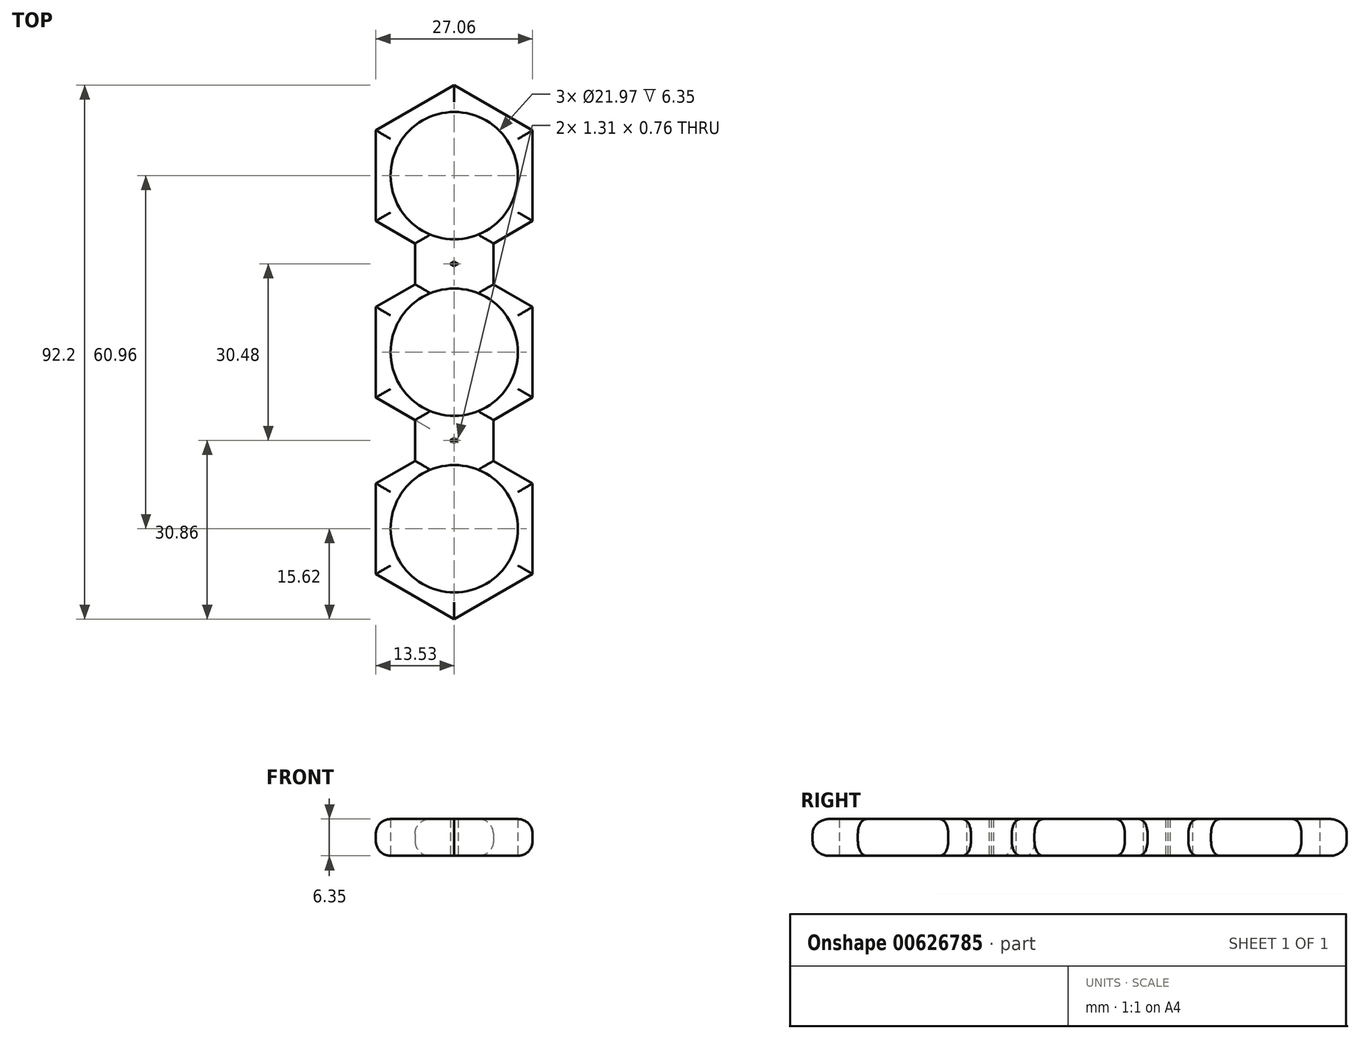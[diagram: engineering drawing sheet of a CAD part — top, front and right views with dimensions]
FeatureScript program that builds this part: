
annotation { "Feature Type Name" : "Feature", "Feature Type Description" : "" }
export const myFeature = defineFeature(function(context is Context, id is Id, definition is map)
    precondition{}
    {
        {
            var Q0;
            Q0=qCreatedBy(makeId("Top.planeOp"),FACE);
            var sketch = newSketch(context, id + "F0", { "sketchPlane" : qUnion([Q0])});
            skCircle(sketch, "E0", {"center": v(0, 0) * mm, "radius": 13.53 * mm});
            skLineSegment(sketch, "E1", {"start": v(0, 0) * mm, "end": v(0, 30.48) * mm});
            skLineSegment(sketch, "E2", {"start": v(0, 0) * mm, "end": v(0, -30.48) * mm});
            skCircle(sketch, "E3", {"center": v(0, 30.48) * mm, "radius": 13.53 * mm});
            skCircle(sketch, "E4", {"center": v(0, -30.48) * mm, "radius": 13.53 * mm});
            skCircle(sketch, "E5", {"center": v(0, 30.48) * mm, "radius": 10.99 * mm});
            skCircle(sketch, "E6", {"center": v(0, 0) * mm, "radius": 10.99 * mm});
            skCircle(sketch, "E7", {"center": v(0, -30.48) * mm, "radius": 10.99 * mm});
            skCircle(sketch, "E8.cCircle", {"center": v(0, 30.48) * mm, "radius": 13.53 * mm, "construction": true});
            skLineSegment(sketch, "E8.0", {"start": v(13.53, 38.29) * mm, "end": v(13.53, 22.67) * mm});
            skLineSegment(sketch, "E8.1", {"start": v(13.53, 22.67) * mm, "end": v(0, 14.86) * mm});
            skLineSegment(sketch, "E8.2", {"start": v(0, 14.86) * mm, "end": v(-13.53, 22.67) * mm});
            skLineSegment(sketch, "E8.3", {"start": v(-13.53, 22.67) * mm, "end": v(-13.53, 38.29) * mm});
            skLineSegment(sketch, "E8.4", {"start": v(-13.53, 38.29) * mm, "end": v(0, 46.1) * mm});
            skLineSegment(sketch, "E8.5", {"start": v(0, 46.1) * mm, "end": v(13.53, 38.29) * mm});
            skPoint(sketch, "E8.0.midPoint", {"position": v(13.53, 30.48) * mm});
            skCircle(sketch, "E9.cCircle", {"center": v(0, 0) * mm, "radius": 13.53 * mm, "construction": true});
            skLineSegment(sketch, "E9.0", {"start": v(13.53, 7.8) * mm, "end": v(13.53, -7.8) * mm});
            skLineSegment(sketch, "E9.1", {"start": v(13.53, -7.8) * mm, "end": v(0, -15.62) * mm});
            skLineSegment(sketch, "E9.2", {"start": v(0, -15.62) * mm, "end": v(-13.53, -7.8) * mm});
            skLineSegment(sketch, "E9.3", {"start": v(-13.53, -7.8) * mm, "end": v(-13.53, 7.8) * mm});
            skLineSegment(sketch, "E9.4", {"start": v(-13.53, 7.8) * mm, "end": v(0, 15.62) * mm});
            skLineSegment(sketch, "E9.5", {"start": v(0, 15.62) * mm, "end": v(13.53, 7.8) * mm});
            skPoint(sketch, "E9.0.midPoint", {"position": v(13.53, 0) * mm});
            skCircle(sketch, "E10.cCircle", {"center": v(0, -30.48) * mm, "radius": 13.53 * mm, "construction": true});
            skLineSegment(sketch, "E10.0", {"start": v(13.53, -22.67) * mm, "end": v(13.53, -38.29) * mm});
            skLineSegment(sketch, "E10.1", {"start": v(13.53, -38.29) * mm, "end": v(0, -46.1) * mm});
            skLineSegment(sketch, "E10.2", {"start": v(0, -46.1) * mm, "end": v(-13.53, -38.29) * mm});
            skLineSegment(sketch, "E10.3", {"start": v(-13.53, -38.29) * mm, "end": v(-13.53, -22.67) * mm});
            skLineSegment(sketch, "E10.4", {"start": v(-13.53, -22.67) * mm, "end": v(0, -14.86) * mm});
            skLineSegment(sketch, "E10.5", {"start": v(0, -14.86) * mm, "end": v(13.53, -22.67) * mm});
            skPoint(sketch, "E10.0.midPoint", {"position": v(13.53, -30.48) * mm});
            skLineSegment(sketch, "E11", {"start": v(-6.76, 18.77) * mm, "end": v(-6.76, 11.71) * mm});
            skLineSegment(sketch, "E12", {"start": v(6.76, 18.77) * mm, "end": v(6.76, 11.71) * mm});
            skLineSegment(sketch, "E13", {"start": v(-6.76, -11.71) * mm, "end": v(-6.76, -18.77) * mm});
            skLineSegment(sketch, "E14", {"start": v(6.76, -11.71) * mm, "end": v(6.76, -18.77) * mm});
            skSolve(sketch);
        }
        {
            var Q0;
            Q0 = qSketchRegion(id + "F0", true);
            extrude(context, id + "F1", {"entities" : qUnion([Q0]), "depth" : 6.35 * mm, "offsetDistance" : 25.4 * mm});
        }
        {
            var Q0;
            Q0=makeQuery(id+"F1.opExtrude","CAP_EDGE",EDGE,{"disambiguationData":[OSD([sQuery(id+"F0.wireOp",EDGE,"E10.2")])],"isStart":false});
            var Q1;
            Q1=makeQuery(id+"F1.opExtrude","CAP_EDGE",EDGE,{"disambiguationData":[OSD([sQuery(id+"F0.wireOp",EDGE,"E10.1")])],"isStart":false});
            var Q2;
            Q2=makeQuery(id+"F1.opExtrude","CAP_EDGE",EDGE,{"disambiguationData":[OSD([sQuery(id+"F0.wireOp",EDGE,"E10.0")])],"isStart":false});
            var Q3;
            Q3=makeQuery(id+"F1.opExtrude","CAP_EDGE",EDGE,{"disambiguationData":[OSD([sQuery(id+"F0.wireOp",EDGE,"E10.3")])],"isStart":false});
            var Q4;
            {var subQ0=sQuery(id+"F0.wireOp",EDGE,"E10.4");Q4=makeQuery(id+"F1.opExtrude","CAP_EDGE",EDGE,{"disambiguationData":[OSD([subQ0]),TDD([makeQuery(id+"F0.imprint","IMPRINT",EDGE,{"disambiguationData":[TD([[makeQuery(id+"F0.imprint","INTERSECT",VERTEX,{"derivedFrom":[sQuery(id+"F0.wireOp",EDGE,"E10.3"),subQ0]}),-1.0]])],"derivedFrom":subQ0})])],"isStart":false});}
            var Q5;
            Q5=makeQuery(id+"F1.opExtrude","CAP_EDGE",EDGE,{"disambiguationData":[OSD([sQuery(id+"F0.wireOp",EDGE,"E13")])],"isStart":false});
            var Q6;
            {var subQ0=sQuery(id+"F0.wireOp",EDGE,"E10.5");Q6=makeQuery(id+"F1.opExtrude","CAP_EDGE",EDGE,{"disambiguationData":[OSD([subQ0]),TDD([makeQuery(id+"F0.imprint","IMPRINT",EDGE,{"disambiguationData":[TD([[makeQuery(id+"F0.imprint","INTERSECT",VERTEX,{"derivedFrom":[sQuery(id+"F0.wireOp",EDGE,"E10.0"),subQ0]}),1.0]])],"derivedFrom":subQ0})])],"isStart":false});}
            var Q7;
            Q7=makeQuery(id+"F1.opExtrude","CAP_EDGE",EDGE,{"disambiguationData":[OSD([sQuery(id+"F0.wireOp",EDGE,"E14")])],"isStart":false});
            var Q8;
            {var subQ0=sQuery(id+"F0.wireOp",EDGE,"E9.2");Q8=makeQuery(id+"F1.opExtrude","CAP_EDGE",EDGE,{"disambiguationData":[OSD([subQ0]),TDD([makeQuery(id+"F0.imprint","IMPRINT",EDGE,{"disambiguationData":[TD([[makeQuery(id+"F0.imprint","INTERSECT",VERTEX,{"derivedFrom":[subQ0,sQuery(id+"F0.wireOp",EDGE,"E9.3")]}),1.0]])],"derivedFrom":subQ0})])],"isStart":false});}
            var Q9;
            Q9=makeQuery(id+"F1.opExtrude","CAP_EDGE",EDGE,{"disambiguationData":[OSD([sQuery(id+"F0.wireOp",EDGE,"E9.3")])],"isStart":false});
            var Q10;
            {var subQ0=sQuery(id+"F0.wireOp",EDGE,"E9.4");Q10=makeQuery(id+"F1.opExtrude","CAP_EDGE",EDGE,{"disambiguationData":[OSD([subQ0]),TDD([makeQuery(id+"F0.imprint","IMPRINT",EDGE,{"disambiguationData":[TD([[makeQuery(id+"F0.imprint","INTERSECT",VERTEX,{"derivedFrom":[sQuery(id+"F0.wireOp",EDGE,"E9.3"),subQ0]}),-1.0]])],"derivedFrom":subQ0})])],"isStart":false});}
            var Q11;
            Q11=makeQuery(id+"F1.opExtrude","CAP_EDGE",EDGE,{"disambiguationData":[OSD([sQuery(id+"F0.wireOp",EDGE,"E11")])],"isStart":false});
            var Q12;
            {var subQ0=sQuery(id+"F0.wireOp",EDGE,"E8.2");Q12=makeQuery(id+"F1.opExtrude","CAP_EDGE",EDGE,{"disambiguationData":[OSD([subQ0]),TDD([makeQuery(id+"F0.imprint","IMPRINT",EDGE,{"disambiguationData":[TD([[makeQuery(id+"F0.imprint","INTERSECT",VERTEX,{"derivedFrom":[subQ0,sQuery(id+"F0.wireOp",EDGE,"E8.3")]}),1.0]])],"derivedFrom":subQ0})])],"isStart":false});}
            var Q13;
            Q13=makeQuery(id+"F1.opExtrude","CAP_EDGE",EDGE,{"disambiguationData":[OSD([sQuery(id+"F0.wireOp",EDGE,"E8.3")])],"isStart":false});
            var Q14;
            Q14=makeQuery(id+"F1.opExtrude","CAP_EDGE",EDGE,{"disambiguationData":[OSD([sQuery(id+"F0.wireOp",EDGE,"E8.4")])],"isStart":false});
            var Q15;
            Q15=makeQuery(id+"F1.opExtrude","CAP_EDGE",EDGE,{"disambiguationData":[OSD([sQuery(id+"F0.wireOp",EDGE,"E8.5")])],"isStart":false});
            var Q16;
            Q16=makeQuery(id+"F1.opExtrude","CAP_EDGE",EDGE,{"disambiguationData":[OSD([sQuery(id+"F0.wireOp",EDGE,"E8.0")])],"isStart":false});
            var Q17;
            Q17=makeQuery(id+"F1.opExtrude","CAP_EDGE",EDGE,{"disambiguationData":[OSD([sQuery(id+"F0.wireOp",EDGE,"E12")])],"isStart":false});
            var Q18;
            {var subQ0=sQuery(id+"F0.wireOp",EDGE,"E8.1");Q18=makeQuery(id+"F1.opExtrude","CAP_EDGE",EDGE,{"disambiguationData":[OSD([subQ0]),TDD([makeQuery(id+"F0.imprint","IMPRINT",EDGE,{"disambiguationData":[TD([[makeQuery(id+"F0.imprint","INTERSECT",VERTEX,{"derivedFrom":[sQuery(id+"F0.wireOp",EDGE,"E8.0"),subQ0]}),-1.0]])],"derivedFrom":subQ0})])],"isStart":false});}
            var Q19;
            {var subQ0=sQuery(id+"F0.wireOp",EDGE,"E9.5");Q19=makeQuery(id+"F1.opExtrude","CAP_EDGE",EDGE,{"disambiguationData":[OSD([subQ0]),TDD([makeQuery(id+"F0.imprint","IMPRINT",EDGE,{"disambiguationData":[TD([[makeQuery(id+"F0.imprint","INTERSECT",VERTEX,{"derivedFrom":[sQuery(id+"F0.wireOp",EDGE,"E9.0"),subQ0]}),1.0]])],"derivedFrom":subQ0})])],"isStart":false});}
            var Q20;
            {var subQ0=sQuery(id+"F0.wireOp",EDGE,"E9.1");Q20=makeQuery(id+"F1.opExtrude","CAP_EDGE",EDGE,{"disambiguationData":[OSD([subQ0]),TDD([makeQuery(id+"F0.imprint","IMPRINT",EDGE,{"disambiguationData":[TD([[makeQuery(id+"F0.imprint","INTERSECT",VERTEX,{"derivedFrom":[sQuery(id+"F0.wireOp",EDGE,"E9.0"),subQ0]}),-1.0]])],"derivedFrom":subQ0})])],"isStart":false});}
            var Q21;
            Q21=makeQuery(id+"F1.opExtrude","CAP_EDGE",EDGE,{"disambiguationData":[OSD([sQuery(id+"F0.wireOp",EDGE,"E9.0")])],"isStart":false});
            var Q22;
            Q22=makeQuery(id+"F1.opExtrude","CAP_EDGE",EDGE,{"disambiguationData":[OSD([sQuery(id+"F0.wireOp",EDGE,"E10.3")])],"isStart":true});
            var Q23;
            Q23=makeQuery(id+"F1.opExtrude","CAP_EDGE",EDGE,{"disambiguationData":[OSD([sQuery(id+"F0.wireOp",EDGE,"E10.2")])],"isStart":true});
            var Q24;
            Q24=makeQuery(id+"F1.opExtrude","CAP_EDGE",EDGE,{"disambiguationData":[OSD([sQuery(id+"F0.wireOp",EDGE,"E10.1")])],"isStart":true});
            var Q25;
            Q25=makeQuery(id+"F1.opExtrude","CAP_EDGE",EDGE,{"disambiguationData":[OSD([sQuery(id+"F0.wireOp",EDGE,"E10.0")])],"isStart":true});
            var Q26;
            {var subQ0=sQuery(id+"F0.wireOp",EDGE,"E10.5");Q26=makeQuery(id+"F1.opExtrude","CAP_EDGE",EDGE,{"disambiguationData":[OSD([subQ0]),TDD([makeQuery(id+"F0.imprint","IMPRINT",EDGE,{"disambiguationData":[TD([[makeQuery(id+"F0.imprint","INTERSECT",VERTEX,{"derivedFrom":[sQuery(id+"F0.wireOp",EDGE,"E10.0"),subQ0]}),1.0]])],"derivedFrom":subQ0})])],"isStart":true});}
            var Q27;
            Q27=makeQuery(id+"F1.opExtrude","CAP_EDGE",EDGE,{"disambiguationData":[OSD([sQuery(id+"F0.wireOp",EDGE,"E14")])],"isStart":true});
            var Q28;
            {var subQ0=sQuery(id+"F0.wireOp",EDGE,"E10.4");Q28=makeQuery(id+"F1.opExtrude","CAP_EDGE",EDGE,{"disambiguationData":[OSD([subQ0]),TDD([makeQuery(id+"F0.imprint","IMPRINT",EDGE,{"disambiguationData":[TD([[makeQuery(id+"F0.imprint","INTERSECT",VERTEX,{"derivedFrom":[sQuery(id+"F0.wireOp",EDGE,"E10.3"),subQ0]}),-1.0]])],"derivedFrom":subQ0})])],"isStart":true});}
            var Q29;
            Q29=makeQuery(id+"F1.opExtrude","CAP_EDGE",EDGE,{"disambiguationData":[OSD([sQuery(id+"F0.wireOp",EDGE,"E13")])],"isStart":true});
            var Q30;
            Q30=makeQuery(id+"F1.opExtrude","CAP_EDGE",EDGE,{"disambiguationData":[OSD([sQuery(id+"F0.wireOp",EDGE,"E9.3")])],"isStart":true});
            var Q31;
            {var subQ0=sQuery(id+"F0.wireOp",EDGE,"E9.4");Q31=makeQuery(id+"F1.opExtrude","CAP_EDGE",EDGE,{"disambiguationData":[OSD([subQ0]),TDD([makeQuery(id+"F0.imprint","IMPRINT",EDGE,{"disambiguationData":[TD([[makeQuery(id+"F0.imprint","INTERSECT",VERTEX,{"derivedFrom":[sQuery(id+"F0.wireOp",EDGE,"E9.3"),subQ0]}),-1.0]])],"derivedFrom":subQ0})])],"isStart":true});}
            var Q32;
            Q32=makeQuery(id+"F1.opExtrude","CAP_EDGE",EDGE,{"disambiguationData":[OSD([sQuery(id+"F0.wireOp",EDGE,"E11")])],"isStart":true});
            var Q33;
            Q33=makeQuery(id+"F1.opExtrude","CAP_EDGE",EDGE,{"disambiguationData":[OSD([sQuery(id+"F0.wireOp",EDGE,"E8.3")])],"isStart":true});
            var Q34;
            Q34=makeQuery(id+"F1.opExtrude","CAP_EDGE",EDGE,{"disambiguationData":[OSD([sQuery(id+"F0.wireOp",EDGE,"E8.4")])],"isStart":true});
            var Q35;
            Q35=makeQuery(id+"F1.opExtrude","CAP_EDGE",EDGE,{"disambiguationData":[OSD([sQuery(id+"F0.wireOp",EDGE,"E8.5")])],"isStart":true});
            var Q36;
            Q36=makeQuery(id+"F1.opExtrude","CAP_EDGE",EDGE,{"disambiguationData":[OSD([sQuery(id+"F0.wireOp",EDGE,"E8.0")])],"isStart":true});
            var Q37;
            {var subQ0=sQuery(id+"F0.wireOp",EDGE,"E8.1");Q37=makeQuery(id+"F1.opExtrude","CAP_EDGE",EDGE,{"disambiguationData":[OSD([subQ0]),TDD([makeQuery(id+"F0.imprint","IMPRINT",EDGE,{"disambiguationData":[TD([[makeQuery(id+"F0.imprint","INTERSECT",VERTEX,{"derivedFrom":[sQuery(id+"F0.wireOp",EDGE,"E8.0"),subQ0]}),-1.0]])],"derivedFrom":subQ0})])],"isStart":true});}
            var Q38;
            Q38=makeQuery(id+"F1.opExtrude","CAP_EDGE",EDGE,{"disambiguationData":[OSD([sQuery(id+"F0.wireOp",EDGE,"E12")])],"isStart":true});
            var Q39;
            {var subQ0=sQuery(id+"F0.wireOp",EDGE,"E9.5");Q39=makeQuery(id+"F1.opExtrude","CAP_EDGE",EDGE,{"disambiguationData":[OSD([subQ0]),TDD([makeQuery(id+"F0.imprint","IMPRINT",EDGE,{"disambiguationData":[TD([[makeQuery(id+"F0.imprint","INTERSECT",VERTEX,{"derivedFrom":[sQuery(id+"F0.wireOp",EDGE,"E9.0"),subQ0]}),1.0]])],"derivedFrom":subQ0})])],"isStart":true});}
            var Q40;
            {var subQ0=sQuery(id+"F0.wireOp",EDGE,"E9.1");Q40=makeQuery(id+"F1.opExtrude","CAP_EDGE",EDGE,{"disambiguationData":[OSD([subQ0]),TDD([makeQuery(id+"F0.imprint","IMPRINT",EDGE,{"disambiguationData":[TD([[makeQuery(id+"F0.imprint","INTERSECT",VERTEX,{"derivedFrom":[sQuery(id+"F0.wireOp",EDGE,"E9.0"),subQ0]}),-1.0]])],"derivedFrom":subQ0})])],"isStart":true});}
            var Q41;
            Q41=makeQuery(id+"F1.opExtrude","CAP_EDGE",EDGE,{"disambiguationData":[OSD([sQuery(id+"F0.wireOp",EDGE,"E9.0")])],"isStart":true});
            var Q42;
            {var subQ0=sQuery(id+"F0.wireOp",EDGE,"E8.2");Q42=makeQuery(id+"F1.opExtrude","CAP_EDGE",EDGE,{"disambiguationData":[OSD([subQ0]),TDD([makeQuery(id+"F0.imprint","IMPRINT",EDGE,{"disambiguationData":[TD([[makeQuery(id+"F0.imprint","INTERSECT",VERTEX,{"derivedFrom":[subQ0,sQuery(id+"F0.wireOp",EDGE,"E8.3")]}),1.0]])],"derivedFrom":subQ0})])],"isStart":true});}
            fillet(context, id + "F2", {"entities" : qUnion([Q0, Q1, Q2, Q3, Q4, Q5, Q6, Q7, Q8, Q9, Q10, Q11, Q12, Q13, Q14, Q15, Q16, Q17, Q18, Q19, Q20, Q21, Q22, Q23, Q24, Q25, Q26, Q27, Q28, Q29, Q30, Q31, Q32, Q33, Q34, Q35, Q36, Q37, Q38, Q39, Q40, Q41, Q42]), "radius" : 2.54 * mm, "tangentPropagation" : true, "allowEdgeOverflow" : false});
        }
    });
